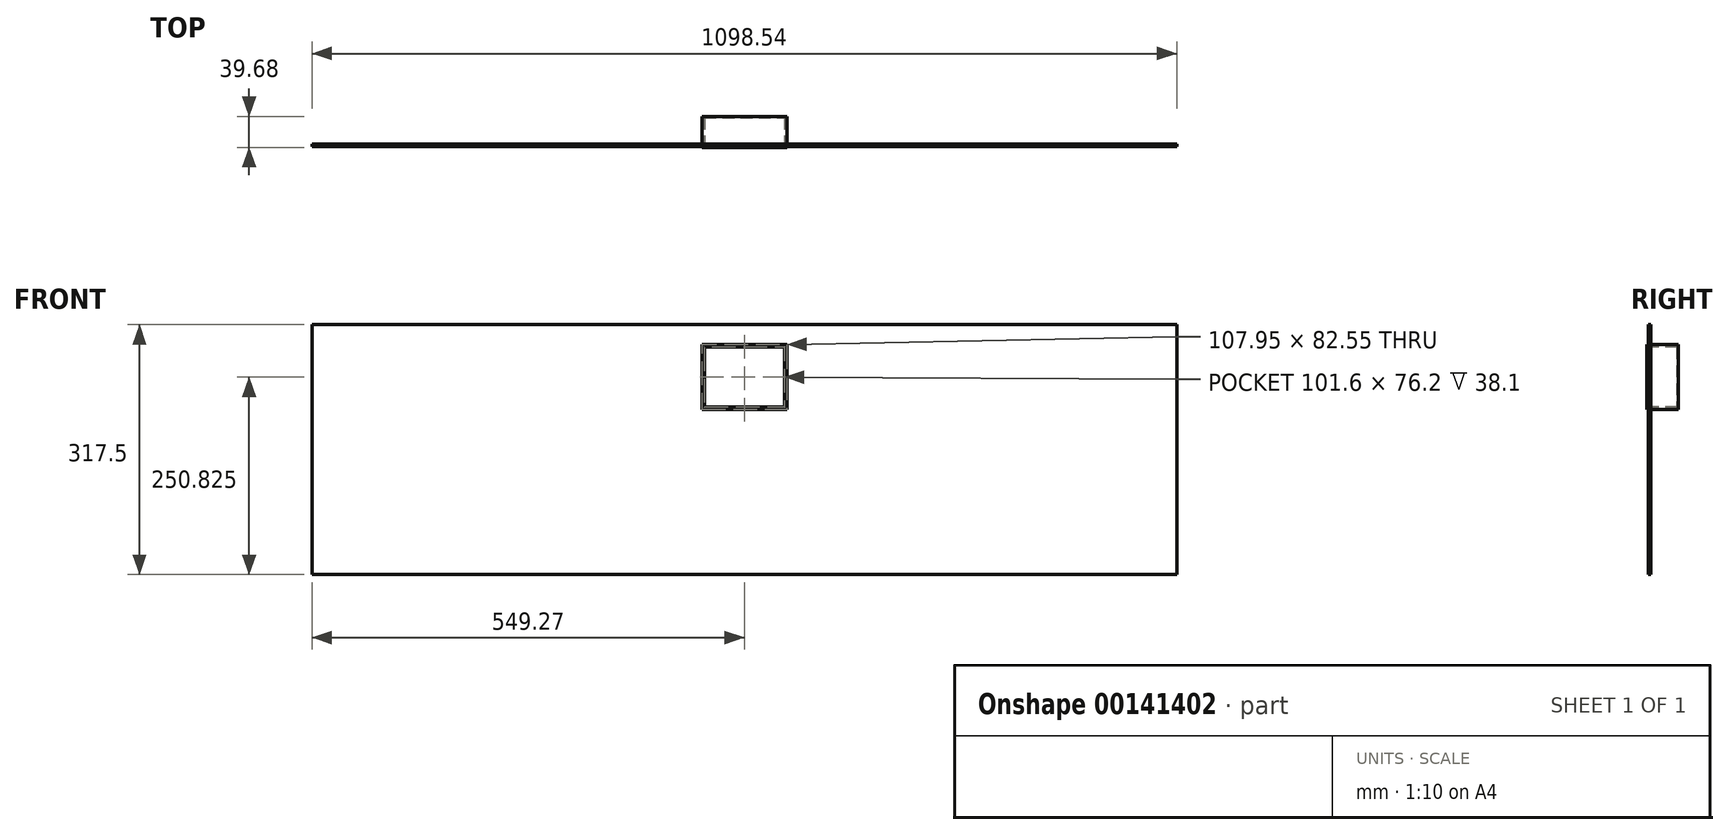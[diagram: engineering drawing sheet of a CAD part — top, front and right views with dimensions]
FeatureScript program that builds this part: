
annotation { "Feature Type Name" : "Feature", "Feature Type Description" : "" }
export const myFeature = defineFeature(function(context is Context, id is Id, definition is map)
    precondition{}
    {
        {
            var Q0;
            Q0=qCreatedBy(makeId("Front.planeOp"),FACE);
            var sketch = newSketch(context, id + "F0", { "sketchPlane" : qUnion([Q0])});
            skLineSegment(sketch, "E0.bottom", {"start": v(-549.28, 158.75) * mm, "end": v(549.27, 158.75) * mm});
            skLineSegment(sketch, "E0.top", {"start": v(-549.28, -158.75) * mm, "end": v(549.27, -158.75) * mm});
            skLineSegment(sketch, "E0.left", {"start": v(-549.28, 158.75) * mm, "end": v(-549.28, -158.75) * mm});
            skLineSegment(sketch, "E0.right", {"start": v(549.27, 158.75) * mm, "end": v(549.27, -158.75) * mm});
            skPoint(sketch, "E0.middle", {"position": v(0, 0) * mm});
            skSolve(sketch);
        }
        {
            var Q0;
            Q0=makeQuery(id+"F0.imprint","IMPRINT",FACE,{"disambiguationData":[TD([[makeQuery(id+"F0.imprint","IMPRINT",EDGE,{"derivedFrom":sQuery(id+"F0.wireOp",EDGE,"E0.bottom")}),-1.0]])]});
            extrude(context, id + "F1", {"entities" : qUnion([Q0]), "depth" : 3.17 * mm});
        }
        {
            var Q0;
            Q0=makeQuery(id+"F1.opExtrude","CAP_FACE",FACE,{"disambiguationData":[OSD([sQuery(id+"F0.wireOp",EDGE,"E0.bottom"),sQuery(id+"F0.wireOp",EDGE,"E0.top"),sQuery(id+"F0.wireOp",EDGE,"E0.left"),sQuery(id+"F0.wireOp",EDGE,"E0.right")])],"isStart":false});
            var sketch = newSketch(context, id + "F2", { "sketchPlane" : qUnion([Q0])});
            skLineSegment(sketch, "E1.bottom", {"start": v(-53.98, 133.35) * mm, "end": v(53.97, 133.35) * mm});
            skLineSegment(sketch, "E1.top", {"start": v(-53.98, 50.8) * mm, "end": v(53.97, 50.8) * mm});
            skLineSegment(sketch, "E1.left", {"start": v(-53.98, 133.35) * mm, "end": v(-53.98, 50.8) * mm});
            skLineSegment(sketch, "E1.right", {"start": v(53.98, 133.35) * mm, "end": v(53.98, 50.8) * mm});
            skPoint(sketch, "E1.middle", {"position": v(0, 92.08) * mm});
            skSolve(sketch);
        }
        {
            var Q0;
            Q0=qSketchRegion(id+"F2",true);
            extrude(context, id + "F3", {"entities" : qUnion([Q0]), "operationType" : NewBodyOperationType.ADD, "oppositeDirection" : true, "depth" : 38.1 * mm});
        }
        {
            var Q0;
            Q0=qSketchRegion(id+"F2",true);
            extrude(context, id + "F4", {"entities" : qUnion([Q0]), "operationType" : NewBodyOperationType.ADD, "depth" : 1.59 * mm});
        }
        {
            var Q0;
            Q0=makeQuery(id+"F4.opExtrude","CAP_FACE",FACE,{"disambiguationData":[OSD([sQuery(id+"F2.wireOp",EDGE,"E1.bottom"),sQuery(id+"F2.wireOp",EDGE,"E1.top"),sQuery(id+"F2.wireOp",EDGE,"E1.left"),sQuery(id+"F2.wireOp",EDGE,"E1.right")])],"isStart":false});
            var sketch = newSketch(context, id + "F5", { "sketchPlane" : qUnion([Q0])});
            skLineSegment(sketch, "E2.bottom", {"start": v(-50.8, 130.18) * mm, "end": v(50.8, 130.18) * mm});
            skLineSegment(sketch, "E2.top", {"start": v(-50.8, 53.98) * mm, "end": v(50.8, 53.98) * mm});
            skLineSegment(sketch, "E2.left", {"start": v(-50.8, 130.18) * mm, "end": v(-50.8, 53.98) * mm});
            skLineSegment(sketch, "E2.right", {"start": v(50.8, 130.18) * mm, "end": v(50.8, 53.98) * mm});
            skPoint(sketch, "E2.middle", {"position": v(0, 92.08) * mm});
            skSolve(sketch);
        }
        {
            var Q0;
            Q0=makeQuery(id+"F5.imprint","IMPRINT",FACE,{"disambiguationData":[TD([[makeQuery(id+"F5.imprint","IMPRINT",EDGE,{"derivedFrom":sQuery(id+"F5.wireOp",EDGE,"E2.bottom")}),-1.0]])]});
            extrude(context, id + "F6", {"entities" : qUnion([Q0]), "operationType" : NewBodyOperationType.REMOVE, "oppositeDirection" : true, "depth" : 38.1 * mm});
        }
    });
